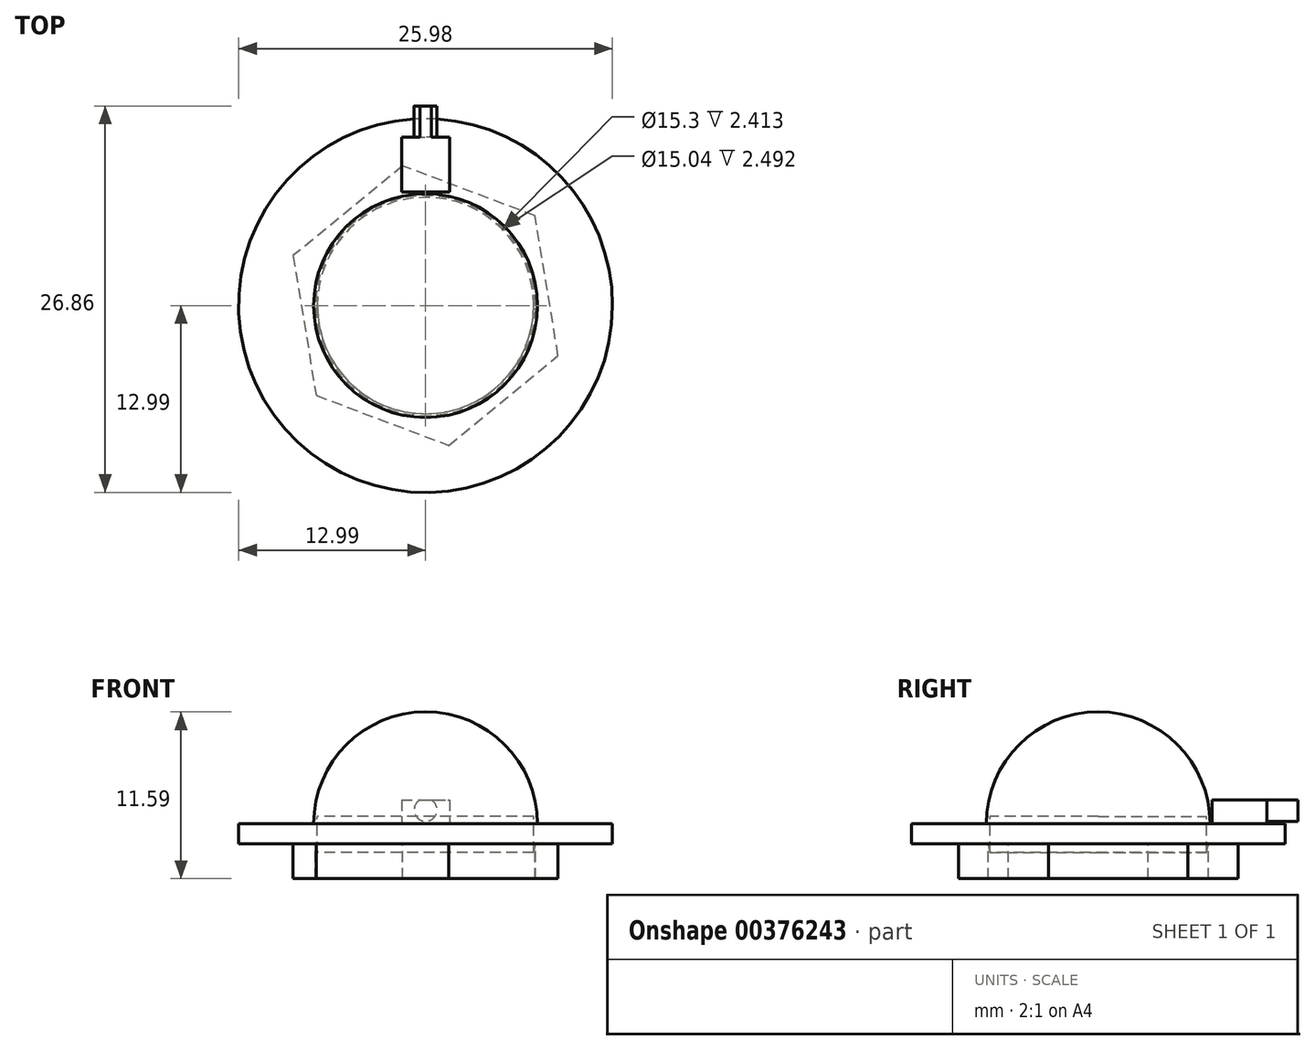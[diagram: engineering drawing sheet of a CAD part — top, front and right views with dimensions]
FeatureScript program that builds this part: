
annotation { "Feature Type Name" : "Feature", "Feature Type Description" : "" }
export const myFeature = defineFeature(function(context is Context, id is Id, definition is map)
    precondition{}
    {
        {
            var Q0;
            Q0=qCreatedBy(makeId("Top.planeOp"),FACE);
            var sketch = newSketch(context, id + "F0", { "sketchPlane" : qUnion([Q0])});
            skArc(sketch, "E0", {"start": v(0, 15.55) * mm, "mid": v(-15.55, 0) * mm, "end": v(0, -15.55) * mm});
            skLineSegment(sketch, "E1", {"start": v(0, 18.06) * mm, "end": v(0, -18.09) * mm});
            skSolve(sketch);
        }
        {
            var Q0;
            Q0=qCreatedBy(makeId("Front.planeOp"),FACE);
            var sketch = newSketch(context, id + "F1", { "sketchPlane" : qUnion([Q0])});
            skCircle(sketch, "E2", {"center": v(0, 0) * mm, "radius": 15.7 * mm});
            skSolve(sketch);
        }
        {
            var Q0;
            {var subQ0=sQuery(id+"F0.wireOp",EDGE,"E0");Q0=makeQuery(id+"F0.imprint","IMPRINT",FACE,{"disambiguationData":[TD([[makeQuery(id+"F0.imprint","IMPRINT",EDGE,{"derivedFrom":subQ0}),1.0]])]});}
            var Q1;
            Q1=sQuery(id+"F1.wireOp",EDGE,"E2");
            revolve(context, id + "F2", {"entities" : qUnion([Q0]), "axis" : qUnion([Q1]), "revolveType" : RevolveType.FULL});
        }
        {
            var Q0;
            Q0=qCreatedBy(makeId("Top.planeOp"),FACE);
            var sketch = newSketch(context, id + "F3", { "sketchPlane" : qUnion([Q0])});
            skCircle(sketch, "E3", {"center": v(0, 0) * mm, "radius": 25.98 * mm});
            skSolve(sketch);
        }
        {
            var Q0;
            Q0=makeQuery(id+"F3.imprint","IMPRINT",FACE,{"disambiguationData":[TD([[makeQuery(id+"F3.imprint","IMPRINT",EDGE,{"derivedFrom":sQuery(id+"F3.wireOp",EDGE,"E3")}),1.0]])]});
            extrude(context, id + "F4", {"entities" : qUnion([Q0]), "operationType" : NewBodyOperationType.ADD, "oppositeDirection" : true, "depth" : 2.8 * mm});
        }
        {
            var Q0;
            Q0=makeQuery(id+"F4.opExtrude","CAP_FACE",FACE,{"disambiguationData":[OSD([sQuery(id+"F3.wireOp",EDGE,"E3")])],"isStart":false});
            var sketch = newSketch(context, id + "F5", { "sketchPlane" : qUnion([Q0])});
            skCircle(sketch, "E4.cCircle", {"center": v(0, 0) * mm, "radius": 19.68 * mm, "construction": true});
            skLineSegment(sketch, "E4.0", {"start": v(-15.22, 12.48) * mm, "end": v(3.2, 19.42) * mm});
            skLineSegment(sketch, "E4.1", {"start": v(3.2, 19.42) * mm, "end": v(18.42, 6.94) * mm});
            skLineSegment(sketch, "E4.2", {"start": v(18.42, 6.94) * mm, "end": v(15.22, -12.48) * mm});
            skLineSegment(sketch, "E4.3", {"start": v(15.22, -12.48) * mm, "end": v(-3.2, -19.42) * mm});
            skLineSegment(sketch, "E4.4", {"start": v(-3.2, -19.42) * mm, "end": v(-18.42, -6.94) * mm});
            skLineSegment(sketch, "E4.5", {"start": v(-18.42, -6.94) * mm, "end": v(-15.22, 12.48) * mm});
            skSolve(sketch);
        }
        {
            var Q0;
            Q0=makeQuery(id+"F5.imprint","IMPRINT",FACE,{"disambiguationData":[TD([[makeQuery(id+"F5.imprint","IMPRINT",EDGE,{"derivedFrom":sQuery(id+"F5.wireOp",EDGE,"E4.0")}),-1.0]])]});
            extrude(context, id + "F6", {"entities" : qUnion([Q0]), "operationType" : NewBodyOperationType.ADD, "depth" : 4.83 * mm});
        }
        {
            var Q0;
            Q0=makeQuery(id+"F6.opExtrude","CAP_FACE",FACE,{"disambiguationData":[OSD([sQuery(id+"F0.wireOp",EDGE,"E0"),sQuery(id+"F3.wireOp",EDGE,"E3"),sQuery(id+"F5.wireOp",EDGE,"E4.0"),sQuery(id+"F5.wireOp",EDGE,"E4.1"),sQuery(id+"F5.wireOp",EDGE,"E4.2"),sQuery(id+"F5.wireOp",EDGE,"E4.3"),sQuery(id+"F5.wireOp",EDGE,"E4.4"),sQuery(id+"F5.wireOp",EDGE,"E4.5")])],"isStart":false});
            var sketch = newSketch(context, id + "F7", { "sketchPlane" : qUnion([Q0])});
            skCircle(sketch, "E5", {"center": v(0, 0) * mm, "radius": 15.04 * mm});
            skSolve(sketch);
        }
        {
            var Q0;
            Q0=makeQuery(id+"F7.imprint","IMPRINT",FACE,{"disambiguationData":[TD([[makeQuery(id+"F7.imprint","IMPRINT",EDGE,{"derivedFrom":sQuery(id+"F7.wireOp",EDGE,"E5")}),1.0]])]});
            extrude(context, id + "F8", {"entities" : qUnion([Q0]), "operationType" : NewBodyOperationType.REMOVE, "depth" : 11.18 * mm, "hasSecondDirection" : true, "secondDirectionOppositeDirection" : true, "secondDirectionDepth" : 8.64 * mm});
        }
        {
            var Q0;
            Q0=makeQuery(id+"F4.opExtrude","CAP_FACE",FACE,{"disambiguationData":[OSD([sQuery(id+"F3.wireOp",EDGE,"E3")])],"isStart":true});
            var sketch = newSketch(context, id + "F9", { "sketchPlane" : qUnion([Q0])});
            skLineSegment(sketch, "E6.bottom", {"start": v(-3.33, 23.42) * mm, "end": v(3.33, 23.42) * mm});
            skLineSegment(sketch, "E6.top", {"start": v(-3.33, 15.81) * mm, "end": v(3.33, 15.81) * mm});
            skLineSegment(sketch, "E6.left", {"start": v(-3.33, 23.42) * mm, "end": v(-3.33, 15.81) * mm});
            skLineSegment(sketch, "E6.right", {"start": v(3.33, 23.42) * mm, "end": v(3.33, 15.81) * mm});
            skPoint(sketch, "E6.middle", {"position": v(0, 19.62) * mm});
            skSolve(sketch);
        }
        {
            var Q0;
            Q0=makeQuery(id+"F9.imprint","IMPRINT",FACE,{"disambiguationData":[TD([[makeQuery(id+"F9.imprint","IMPRINT",EDGE,{"derivedFrom":sQuery(id+"F9.wireOp",EDGE,"E6.bottom")}),-1.0]])]});
            extrude(context, id + "F10", {"entities" : qUnion([Q0]), "operationType" : NewBodyOperationType.ADD, "depth" : 3.3 * mm});
        }
        {
            var Q0;
            Q0=makeQuery(id+"F10.opExtrude","SWEPT_FACE",FACE,{"disambiguationData":[OSD([sQuery(id+"F9.wireOp",EDGE,"E6.bottom")])]});
            var sketch = newSketch(context, id + "F11", { "sketchPlane" : qUnion([Q0])});
            skCircle(sketch, "E7", {"center": v(0, 1.94) * mm, "radius": 1.59 * mm});
            skSolve(sketch);
        }
        {
            var Q0;
            {var subQ0=sQuery(id+"F11.wireOp",EDGE,"E7");var subQ1=makeQuery(id+"F10.opExtrude","CAP_EDGE",EDGE,{"disambiguationData":[OSD([sQuery(id+"F9.wireOp",EDGE,"E6.bottom")])],"isStart":false});var subQ2=makeQuery(id+"F11.imprint","INTERSECT",VERTEX,{"disambiguationData":[OD(0.0)],"derivedFrom":[subQ1,subQ0]});Q0=makeQuery(id+"F11.imprint","IMPRINT",FACE,{"disambiguationData":[TD([[makeQuery(id+"F11.imprint","IMPRINT",EDGE,{"disambiguationData":[TD([[subQ2,1.0]])],"derivedFrom":subQ0}),1.0]])]});}
            extrude(context, id + "F12", {"entities" : qUnion([Q0]), "operationType" : NewBodyOperationType.ADD, "depth" : 4.32 * mm});
        }
        {
            var Q0;
            Q0=makeQuery(id+"F2.opRevolve","SWEPT_BODY",BODY,{"disambiguationData":[OSD([sQuery(id+"F0.wireOp",EDGE,"E0"),sQuery(id+"F0.wireOp",EDGE,"E1")])]});
            var Q1;
            Q1=qCreatedBy(makeId("Origin.pointOp"),VERTEX);
            var Q2;
            Q2=qCreatedBy(makeId("Origin.pointOp"),VERTEX);
            transform(context, id + "F13", {"entities" : qUnion([Q0]), "transformType" : TransformType.SCALE_UNIFORMLY, "scale" : .5, "scalePoint" : qUnion([Q2]), "makeCopy" : false});
        }
    });
